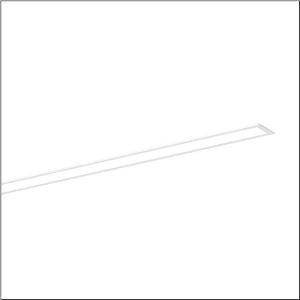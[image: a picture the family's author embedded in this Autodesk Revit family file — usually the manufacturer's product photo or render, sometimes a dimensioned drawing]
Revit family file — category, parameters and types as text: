
# Revit family: silica_r__21_51mx10tct5w_f343
name_source: partatom
category: Lighting Fixtures
units: mm (PartAtom-declared; Revit-internal decimal feet)

## family parameters
Cut with Voids When Loaded = No
Host = Face
Light Source = No
Part Type = Normal
Room Calculation Point = No
Round Connector Dimension = Use Diameter
Shared = No

## types (1)
- --- (1 x LED, 6000 lm, 51.3 W, 6500K)
    Apparent Load = 51 VA
    CIE Flux Codes = 48 79 96 100 100
    Color Rendering = 80
    Color Temperature = 6500K
    Default Elevation = 1800 mm
    Description = Silica® 21, office luminaire, primary optical cover: cover, of PMMA, opal, light emission: direct distribution, primary light characteristic: symmetric, installation type: recessed, LED, rated luminous flux: 6.000lm, luminous efficacy: 112lm/W, light colour: 8tw, colour temperature: 2700..6500K, with terminal, 3+2-pole, max. 2.5mm², mains connection: 220..240V, AC, 50/60Hz, rated input power: 53.8W, luminaire housing, of aluminium, traffic white (RAL 9016), length: 3.028mm, width: 79mm, height: 53mm, protection rating (complete): IP20, insulation class (complete): insulation class I (protective earthing), certification: CE, permissible operating ambient temperature: 0..+35°C, standard: EN 50419, packaging unit: 1 piece
    Height = 0 mm  [stored 0 ft]
    Lamp = 1 x LED
    Lamp Light Flux = 6000 lm
    Lamp Power = 51.3 W
    Lamp count = 1
    Length = 3027 mm
    Luminous efficacy = 117 lm/W
    Manufacturer = Siteco
    ModVariant = No
    Model = 51MX10TCT5W
    Mounting Place = Ceiling
    Mounting Type = Recessed
    Number of Poles = 1
    OnlyDefault = Yes
    Power Factor = 1
    Product Name = Silica® 21
    Product group = office luminaire | ceiling recessed
    ProductGroupID = 401
    Protection Class = Protection class I
    Protection Degree = IP 20
    RLX_Detail_Level = 1
    RLX_Emergency_Light_Flux = 0 lm
    RLX_Emergency_Type = 0
    RLX_Emergency_Type_DB = No
    RlxData = <blob elided: 17889 chars, md5=ba04935d>
    Socket = socket
    Standby Power = 0 W
    System Light Flux = 6000 lm
    System Power = 51 W
    Type Comments = individual setting
    Type Image = l_1313615.jpg
    URL = http://relux.com
    VarID = @adj_089085
    Voltage = 0 V
    Weight = 0.00 kg
    Width = 79 mm

note: [stored X ft] marks values corroborated as IEEE doubles in the binary element streams (Revit-internal decimal feet)

## geometry (parser evidence)
native form markers: Blend x4, Sweep x12
no freeform markers — native parametric forms only
